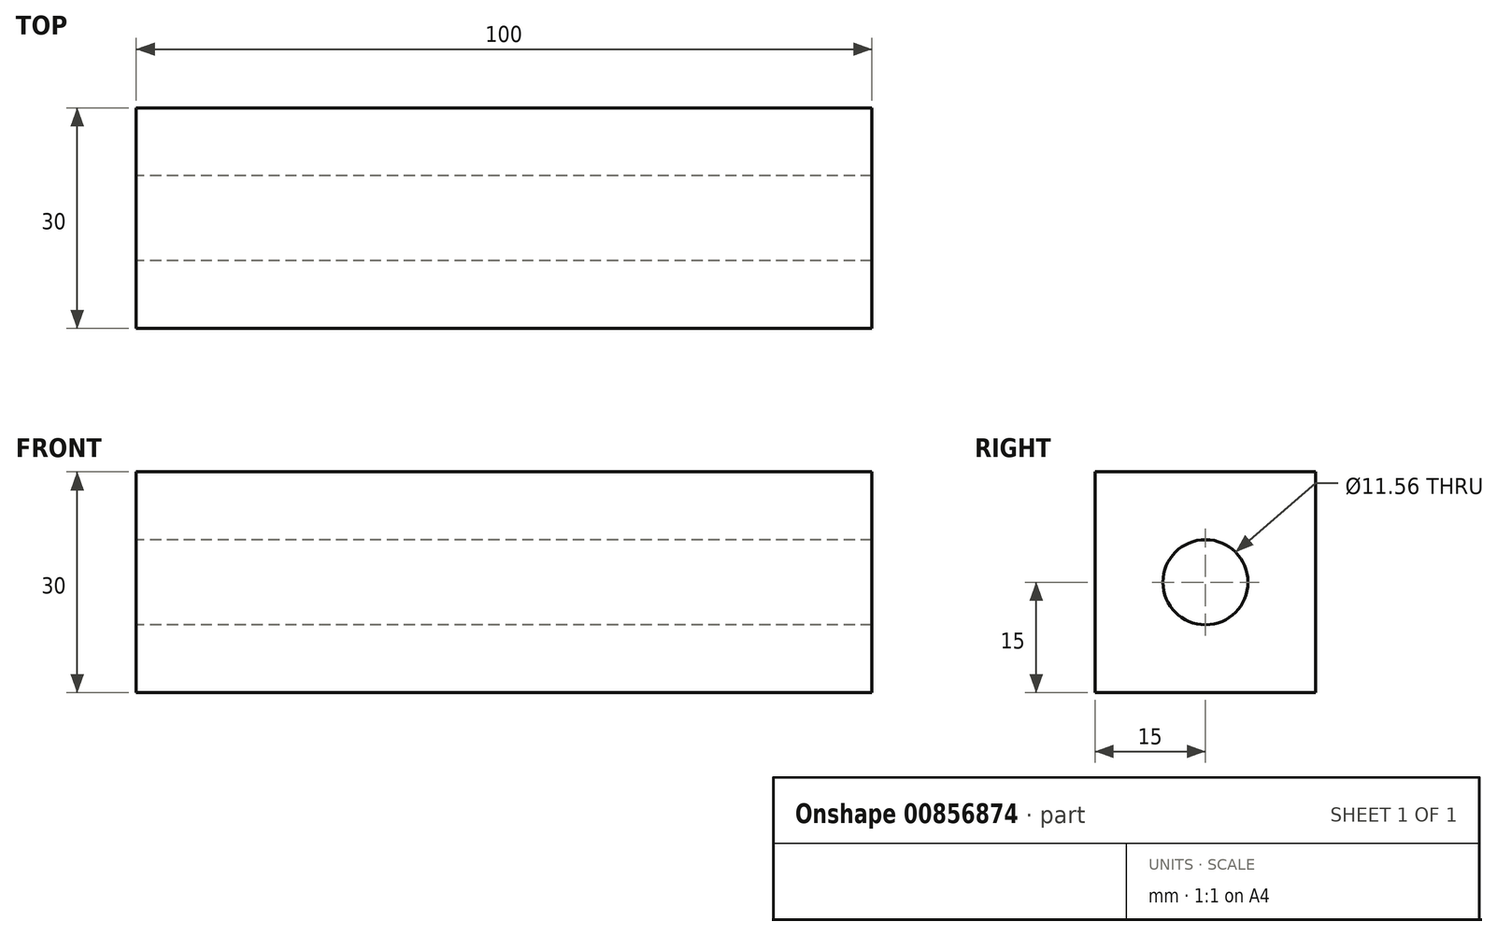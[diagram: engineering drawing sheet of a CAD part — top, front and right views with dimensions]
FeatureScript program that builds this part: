
annotation { "Feature Type Name" : "Feature", "Feature Type Description" : "" }
export const myFeature = defineFeature(function(context is Context, id is Id, definition is map)
    precondition{}
    {
        {
            var Q0;
            Q0=qCreatedBy(makeId("Right.planeOp"),FACE);
            var sketch = newSketch(context, id + "F0", { "sketchPlane" : qUnion([Q0])});
            skLineSegment(sketch, "E0.bottom", {"start": v(-15, 15) * mm, "end": v(15, 15) * mm});
            skLineSegment(sketch, "E0.top", {"start": v(-15, -15) * mm, "end": v(15, -15) * mm});
            skLineSegment(sketch, "E0.left", {"start": v(-15, 15) * mm, "end": v(-15, -15) * mm});
            skLineSegment(sketch, "E0.right", {"start": v(15, 15) * mm, "end": v(15, -15) * mm});
            skPoint(sketch, "E0.middle", {"position": v(0, 0) * mm});
            skSolve(sketch);
        }
        {
            var Q0;
            Q0=makeQuery(id+"F0.imprint","IMPRINT",FACE,{"disambiguationData":[TD([[makeQuery(id+"F0.imprint","IMPRINT",EDGE,{"derivedFrom":sQuery(id+"F0.wireOp",EDGE,"E0.bottom")}),-1.0]])]});
            extrude(context, id + "F1", {"entities" : qUnion([Q0]), "depth" : 100 * mm, "offsetDistance" : 25 * mm});
        }
        {
            var Q0;
            Q0=makeQuery(id+"F1.opExtrude","CAP_FACE",FACE,{"disambiguationData":[OSD([sQuery(id+"F0.wireOp",EDGE,"E0.bottom"),sQuery(id+"F0.wireOp",EDGE,"E0.top"),sQuery(id+"F0.wireOp",EDGE,"E0.left"),sQuery(id+"F0.wireOp",EDGE,"E0.right")])],"isStart":true});
            var sketch = newSketch(context, id + "F2", { "sketchPlane" : qUnion([Q0])});
            skCircle(sketch, "E1", {"center": v(0, 0) * mm, "radius": 5.78 * mm});
            skSolve(sketch);
        }
        {
            var Q0;
            Q0=makeQuery(id+"F2.imprint","IMPRINT",FACE,{"disambiguationData":[TD([[makeQuery(id+"F2.imprint","IMPRINT",EDGE,{"derivedFrom":sQuery(id+"F2.wireOp",EDGE,"E1")}),1.0]])]});
            extrude(context, id + "F3", {"entities" : qUnion([Q0]), "operationType" : NewBodyOperationType.REMOVE, "oppositeDirection" : true, "depth" : 200 * mm, "offsetDistance" : 25 * mm});
        }
    });
